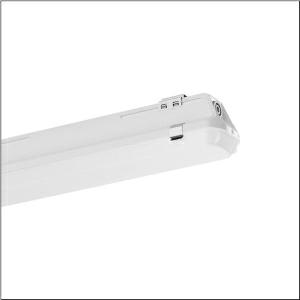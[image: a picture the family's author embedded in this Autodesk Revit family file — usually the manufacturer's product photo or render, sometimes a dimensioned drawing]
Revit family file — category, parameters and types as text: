
# Revit family: monsun_r__11_51fp209p460h_6055
name_source: partatom
category: Lighting Fixtures
units: mm (PartAtom-declared; Revit-internal decimal feet)

## family parameters
Cut with Voids When Loaded = No
Host = Face
Light Source = No
Part Type = Normal
Room Calculation Point = No
Round Connector Dimension = Use Diameter
Shared = No

## types (1)
- Monsun® 11 (1 x LED, 5490 lm, 34 W, 4000K)
    Apparent Load = 34 VA
    CIE Flux Codes = 45 75 93 94 100
    Color Rendering = 80
    Color Temperature = 4000K
    Default Elevation = 1800 mm
    Description = Monsun® 11, damp-proof luminaire, chain hanger, primary optical cover: enclosure, of PC, light emission: direct distribution, primary light characteristic: symmetric, installation type: suspended mounting, surface-mounted, horizontal mounting, vertical mounting, LED, rated luminous flux: 5.490lm, luminous efficacy: 161lm/W, light colour: 840, colour temperature: 4000K, control gear: ECG, with terminal, 3-pole, max. 2.5mm², mains connection: 220..240V, AC, 50/60Hz, rated input power: 34W, luminaire housing, of glass-fibre reinforced polyester, uncoated, bright grey, incl. chain hanger, length: 1.590mm, width: 90mm, height: 88mm, clip for enclosure, of stainless steel (V2A), ceiling mounting element, of stainless steel (V2A), chain hanger, of stainless steel (V2A), protection rating (complete): IP66, insulation class (complete): insulation class I (protective earthing), certification: CE, ENEC, VDE, UKCA, protection symbol: D, impact resistance: IK08, permissible operating ambient temperature: -35..+40°C, standard: EN 50419, EN 60598-2-1, no direct snow, no direct sun, no direct rain, for indoor or canopied outdoor use, corresponds to IFS (International Featured Standards) requirements for safety and quality in the food industry, contact your sales advisor before using the luminaires in applications with unclear chemical exposure, large temperature fluctuations or condensation-forming humidity, LABS conformity tested according to VDMA 24364:2018-05, packaging unit: 1 piece
    Height = 89 mm
    Lamp = 1 x LED
    Lamp Light Flux = 5490 lm
    Lamp Power = 34 W
    Lamp count = 1
    Length = 1590 mm
    Luminous efficacy = 161 lm/W
    Manufacturer = Siteco
    ModVariant = No
    Model = 51FP209P460H
    Mounting Place = Ceiling
    Mounting Type = Surface mounted
    Number of Poles = 1
    OnlyDefault = Yes
    Power Factor = 1
    Product Name = Monsun® 11
    Product group = damp-proof luminaire
    ProductGroupID = 300
    Protection Class = Protection class I
    Protection Degree = IP 66
    RLX_Detail_Level = 1
    RLX_Emergency_Light_Flux = 0 lm
    RLX_Emergency_Type = 0
    RLX_Emergency_Type_DB = No
    RlxData = <blob elided: 88533 chars, md5=46e21955>
    Socket = socket
    Standby Power = 0 W
    System Light Flux = 5490 lm
    System Power = 34 W
    Type Comments = Product without accessories
    Type Image = l_1319650.jpg
    URL = http://relux.com
    VarID = ---
    Voltage = 0 V
    Weight = 0.00 kg
    Width = 90 mm

## geometry (parser evidence)
native form markers: Blend x4, Sweep x12
no freeform markers — native parametric forms only
